# Revit family: Haworth_Enclose_Wall_Solid
name_source: partatom
category: Furniture Systems
revit_build: Autodesk Revit 2018 (Build: 20170223_1515(x64)
units: mm (PartAtom-declared; Revit-internal decimal feet)

## family parameters
Always vertical = Yes
Cut with Voids When Loaded = No
OmniClass Number = 23.25.40.14
OmniClass Title = Demountable Partitions
Part Type = Normal
Room Calculation Point = No
Round Connector Dimension = Use Diameter
Shared = Yes
Work Plane-Based = No

## types (5) — shared parameters
Actual Height = 108 "
Actual Panel 1 Back Height = 32 "
Actual Panel 1 Front Height = 32 "
Actual Panel 2 Back Height = 64 "
Actual Panel 2 Front Height = 64 "
Assembly Code = C1010200
Base Height = 1.25 "
Cap Height = 1 "
Ceiling Mount = Yes
Description = Wall Solid
End of Run Finish = Haworth _ Polymer _ Black
End of Run Width = 0.155 "
Frame Depth = 4 "
Frame Finish = Haworth _ Metal _ Brushed Aluminum
Glass Offset = 4.75 "
Height = 108 "
Horizontal Bottom Adjuster Width = 3.875 "
Horizontal Bottom Trim Width = 2.5 "
Horizontal Frame Width = 0.875 "
Horizontal Top Adjuster Width = 2.625 "
Horizontal Top Trim Width = 1.5 "
Manufacturer = Haworth
Material Options = http://surfaces.haworth.com
Max # of Panels = 3
Max. Height = 144 "
Max. Width = 60 "
Min. Height = 84 "
Min. Width = 8 "
Min/Max Height = 84-144 in.
Min/Max Width = 8-60 in.
Model = Haworth - Enclose
Offset Back = 9.84 "
Offset Front = 9.84 "
Panel 1 Back Height = 32 "
Panel 1 Front Height = 32 "
Panel 2 Back Height = 64 "
Panel 2 Front Height = 64 "
Panel Depth = 0.5 "
Panel Height Back = 97.16 "
Panel Height Front = 97.16 "
Panel Height Note = All Heights are A.F.F.
Panel Size Note = 8in increments
Raceway Finish = Haworth _ Metal _ Brushed Aluminum
Raceway Panel Back = Yes
Raceway Panel Back Height = 8.59 "
Raceway Panel Front = Yes
Raceway Panel Front Height = 8.59 "
Revision Number = 4
Size = Verify Final Dim. w/ Haworth
Sustainability Info = http://www.haworth.com
URL = www.haworth.com
URL - Product = http://www.haworth.com
Vertical Frame Width = 0.875 "
Warranty = http://www.haworth.com

## per-type parameters (varying)
| type | # of Panels Back | # of Panels Front | Actual # of Panels Back | Actual # of Panels Front | Actual Width | Panel Width | Raceway Panel Width | Width |
| 36" x 108" | 1 | 1 | 1 | 1 | 36 " | 35.69 " | 35.69 " | 36 " |
| 24" x 108" | 3 | 3 | 3 | 3 | 24 " | 23.69 " | 23.69 " | 24 " |
| 30" x 108" | 3 | 3 | 3 | 3 | 30 " | 29.69 " | 29.69 " | 30 " |
| 42" x 108" | 3 | 3 | 3 | 3 | 42 " | 41.69 " | 41.69 " | 42 " |
| 48" x 108" | 3 | 3 | 3 | 3 | 48 " | 47.69 " | 47.69 " | 48 " |

## geometry (parser evidence)
native form markers: Sweep x9
no freeform markers — native parametric forms only
